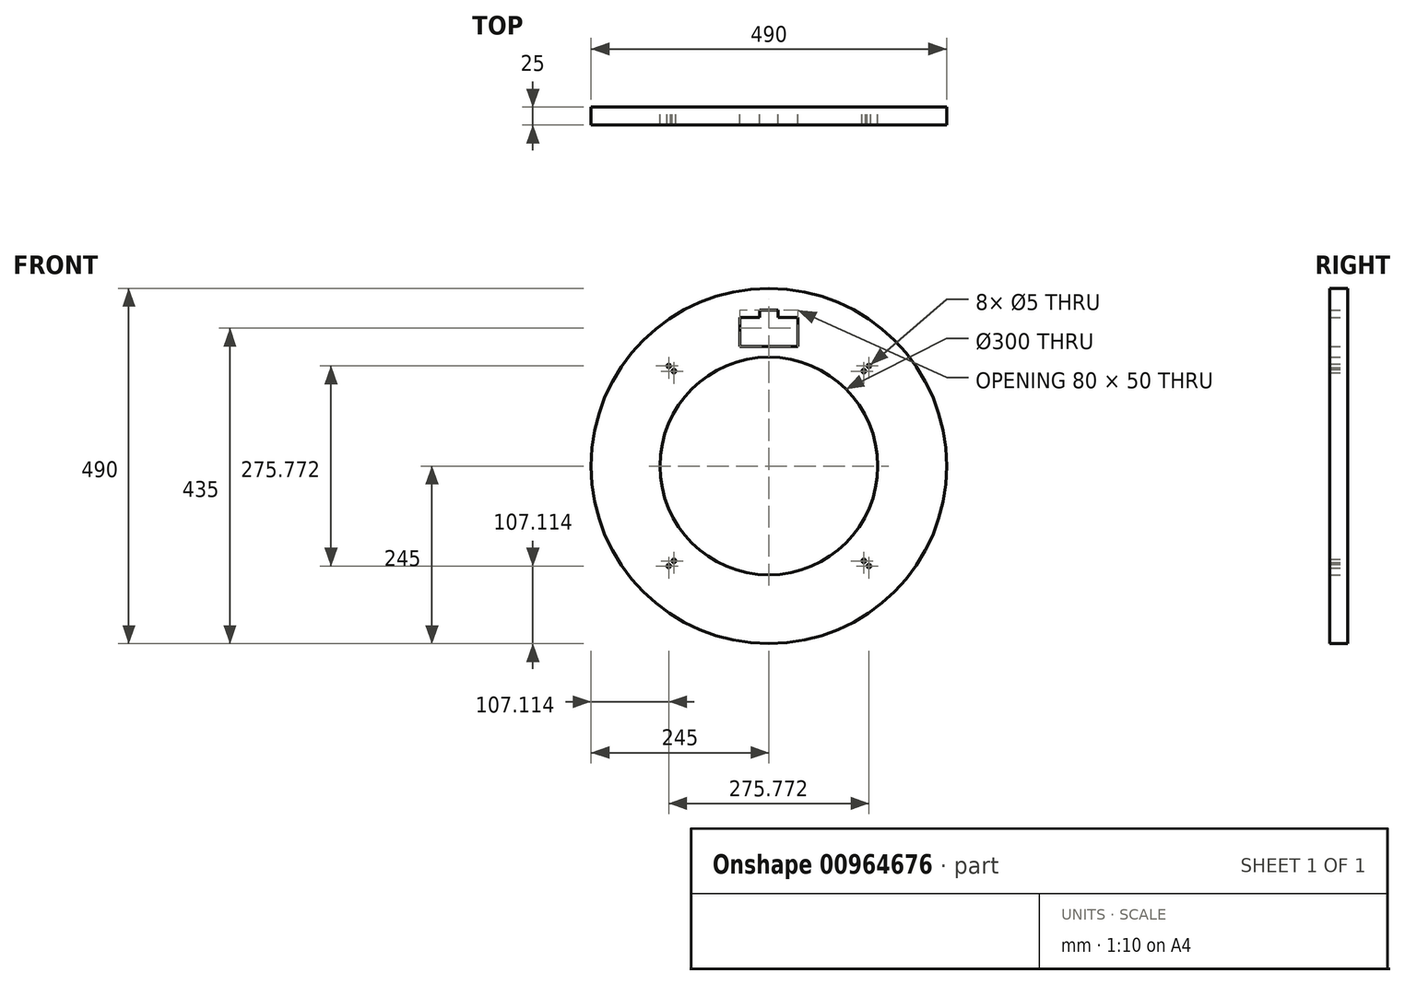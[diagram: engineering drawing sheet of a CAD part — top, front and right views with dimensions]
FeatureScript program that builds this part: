
annotation { "Feature Type Name" : "Feature", "Feature Type Description" : "" }
export const myFeature = defineFeature(function(context is Context, id is Id, definition is map)
    precondition{}
    {
        {
            var Q0;
            Q0=qCreatedBy(makeId("Front.planeOp"),FACE);
            var sketch = newSketch(context, id + "F0", { "sketchPlane" : qUnion([Q0])});
            skCircle(sketch, "E0", {"center": v(0, 0) * mm, "radius": 245 * mm});
            skLineSegment(sketch, "E1.bottom", {"start": v(40, 165) * mm, "end": v(-40, 165) * mm});
            skLineSegment(sketch, "E1.top", {"start": v(40, 205) * mm, "end": v(-40, 205) * mm});
            skLineSegment(sketch, "E1.left", {"start": v(40, 165) * mm, "end": v(40, 205) * mm});
            skLineSegment(sketch, "E1.right", {"start": v(-40, 165) * mm, "end": v(-40, 205) * mm});
            skPoint(sketch, "E1.middle", {"position": v(0, 185) * mm});
            skLineSegment(sketch, "E2", {"start": v(0, 0) * mm, "end": v(0, 245) * mm, "construction": true});
            skLineSegment(sketch, "E3", {"start": v(0, 0) * mm, "end": v(-173.24, 173.24) * mm, "construction": true});
            skCircle(sketch, "E4", {"center": v(-137.89, 137.89) * mm, "radius": 2.5 * mm});
            skCircle(sketch, "E5", {"center": v(-130.81, 130.81) * mm, "radius": 2.5 * mm});
            skCircle(sketch, "E6", {"center": v(0, 0) * mm, "radius": 150 * mm});
            skLineSegment(sketch, "E7", {"start": v(0, 0) * mm, "end": v(173.24, 173.24) * mm, "construction": true});
            skLineSegment(sketch, "E8", {"start": v(0, 0) * mm, "end": v(173.24, -173.24) * mm, "construction": true});
            skLineSegment(sketch, "E9", {"start": v(0, 0) * mm, "end": v(-173.24, -173.24) * mm, "construction": true});
            skCircle(sketch, "E10", {"center": v(130.81, 130.81) * mm, "radius": 2.5 * mm});
            skCircle(sketch, "E11", {"center": v(137.89, 137.89) * mm, "radius": 2.5 * mm});
            skCircle(sketch, "E12", {"center": v(130.81, -130.81) * mm, "radius": 2.5 * mm});
            skCircle(sketch, "E13", {"center": v(137.89, -137.89) * mm, "radius": 2.5 * mm});
            skCircle(sketch, "E14", {"center": v(-137.89, -137.89) * mm, "radius": 2.5 * mm});
            skCircle(sketch, "E15", {"center": v(-130.81, -130.81) * mm, "radius": 2.5 * mm});
            skLineSegment(sketch, "E16", {"start": v(-12.5, 205) * mm, "end": v(-12.5, 215) * mm});
            skLineSegment(sketch, "E17", {"start": v(-12.5, 215) * mm, "end": v(12.5, 215) * mm});
            skLineSegment(sketch, "E18", {"start": v(12.5, 215) * mm, "end": v(12.5, 205) * mm});
            skPoint(sketch, "E19", {"position": v(0, 215) * mm});
            skSolve(sketch);
        }
        {
            var Q0;
            Q0=makeQuery(id+"F0.imprint","IMPRINT",FACE,{"disambiguationData":[TD([[makeQuery(id+"F0.imprint","IMPRINT",EDGE,{"derivedFrom":sQuery(id+"F0.wireOp",EDGE,"E0")}),1.0]])]});
            extrude(context, id + "F1", {"entities" : qUnion([Q0]), "depth" : 25 * mm, "offsetDistance" : 25 * mm});
        }
    });
